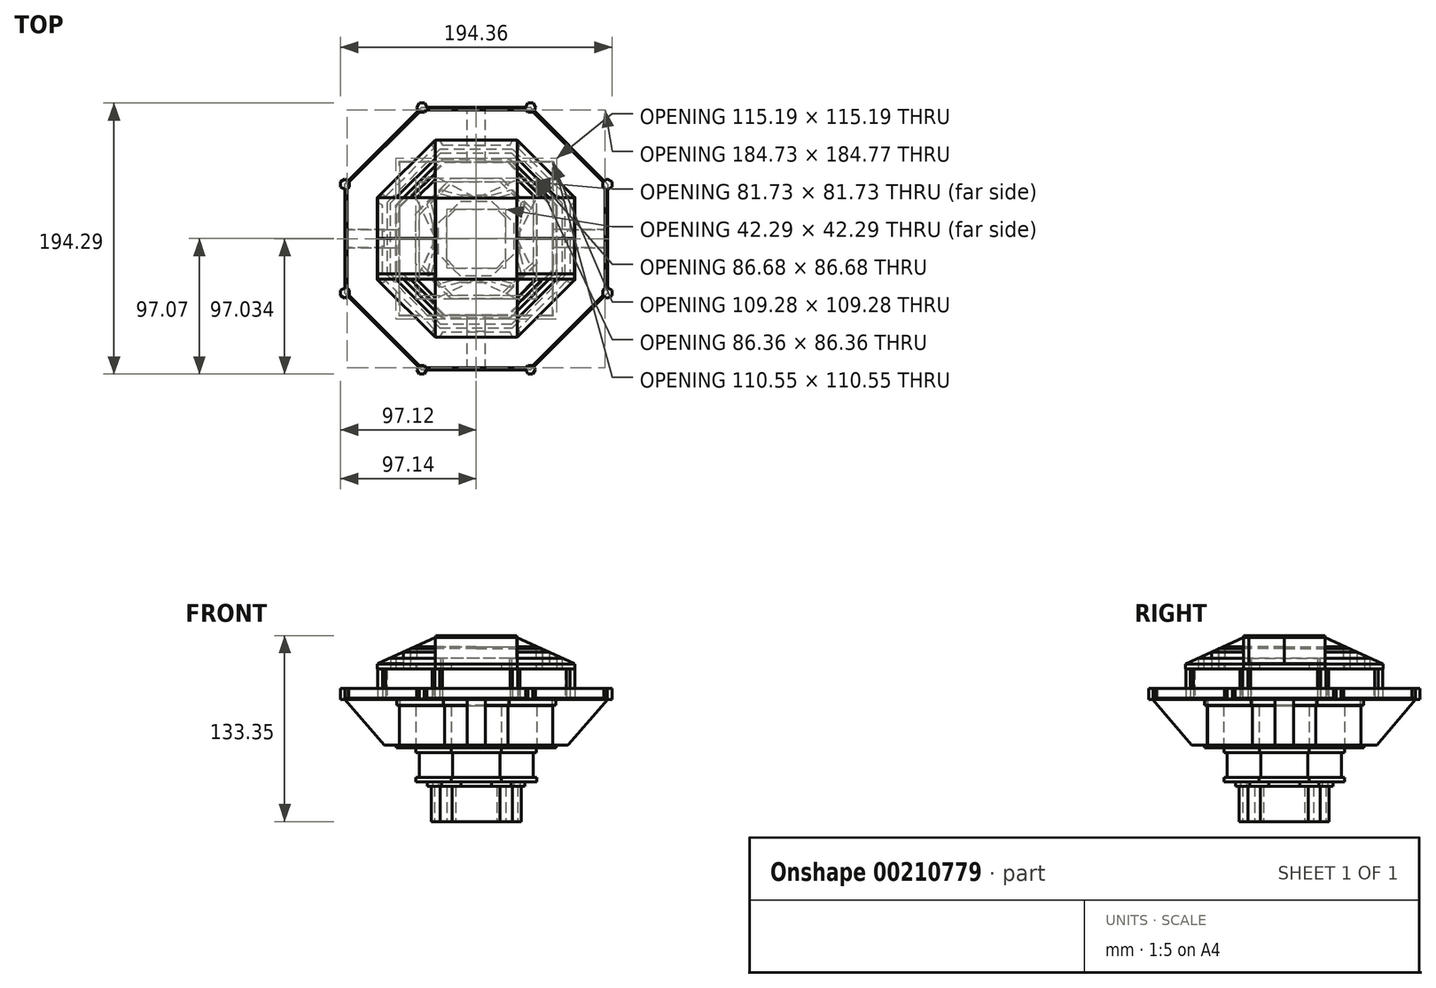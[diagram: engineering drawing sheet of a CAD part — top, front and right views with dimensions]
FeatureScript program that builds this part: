
annotation { "Feature Type Name" : "Feature", "Feature Type Description" : "" }
export const myFeature = defineFeature(function(context is Context, id is Id, definition is map)
    precondition{}
    {
        {
            var Q0;
            Q0=qCreatedBy(makeId("Top.planeOp"),FACE);
            cPlane(context, id + "F0", {"entities" : qUnion([Q0]), "cplaneType" : CPlaneType.OFFSET, "offset" : 31.24 * mm, "width" : 152.4 * mm, "height" : 152.4 * mm});
        }
        {
            var Q0;
            Q0=qCreatedBy(id+"F0.planeOp",FACE);
            cPlane(context, id + "F1", {"entities" : qUnion([Q0]), "cplaneType" : CPlaneType.OFFSET, "offset" : 19.05 * mm, "width" : 152.4 * mm, "height" : 152.4 * mm});
        }
        {
            var Q0;
            Q0=qCreatedBy(id+"F1.planeOp",FACE);
            var sketch = newSketch(context, id + "F2", { "sketchPlane" : qUnion([Q0])});
            skPoint(sketch, "E0.0.midPoint", {"position": v(0, 33.22) * mm});
            skCircle(sketch, "E1.cCircle", {"center": v(-23.49, -23.49) * mm, "radius": 7.84 * mm, "construction": true});
            skLineSegment(sketch, "E1.0", {"start": v(-25.83, -32.23) * mm, "end": v(-32.23, -25.83) * mm});
            skLineSegment(sketch, "E1.1", {"start": v(-32.23, -25.83) * mm, "end": v(-29.89, -17.09) * mm});
            skLineSegment(sketch, "E1.2", {"start": v(-29.89, -17.09) * mm, "end": v(-21.15, -14.75) * mm});
            skLineSegment(sketch, "E1.3", {"start": v(-21.15, -14.75) * mm, "end": v(-14.75, -21.15) * mm});
            skLineSegment(sketch, "E1.4", {"start": v(-14.75, -21.15) * mm, "end": v(-17.09, -29.89) * mm});
            skLineSegment(sketch, "E1.5", {"start": v(-17.09, -29.89) * mm, "end": v(-25.83, -32.23) * mm});
            skPoint(sketch, "E1.0.midPoint", {"position": v(-29.03, -29.03) * mm});
            skCircle(sketch, "E2.cCircle", {"center": v(23.49, -23.49) * mm, "radius": 7.84 * mm, "construction": true});
            skLineSegment(sketch, "E2.0", {"start": v(32.23, -25.83) * mm, "end": v(25.83, -32.23) * mm});
            skLineSegment(sketch, "E2.1", {"start": v(25.83, -32.23) * mm, "end": v(17.09, -29.89) * mm});
            skLineSegment(sketch, "E2.2", {"start": v(17.09, -29.89) * mm, "end": v(14.75, -21.15) * mm});
            skLineSegment(sketch, "E2.3", {"start": v(14.75, -21.15) * mm, "end": v(21.15, -14.75) * mm});
            skLineSegment(sketch, "E2.4", {"start": v(21.15, -14.75) * mm, "end": v(29.89, -17.09) * mm});
            skLineSegment(sketch, "E2.5", {"start": v(29.89, -17.09) * mm, "end": v(32.23, -25.83) * mm});
            skPoint(sketch, "E2.0.midPoint", {"position": v(29.03, -29.03) * mm});
            skCircle(sketch, "E3.cCircle", {"center": v(23.49, 23.49) * mm, "radius": 7.84 * mm, "construction": true});
            skLineSegment(sketch, "E3.0", {"start": v(25.83, 32.23) * mm, "end": v(32.23, 25.83) * mm});
            skLineSegment(sketch, "E3.1", {"start": v(32.23, 25.83) * mm, "end": v(29.89, 17.09) * mm});
            skLineSegment(sketch, "E3.2", {"start": v(29.89, 17.09) * mm, "end": v(21.15, 14.75) * mm});
            skLineSegment(sketch, "E3.3", {"start": v(21.15, 14.75) * mm, "end": v(14.75, 21.15) * mm});
            skLineSegment(sketch, "E3.4", {"start": v(14.75, 21.15) * mm, "end": v(17.09, 29.89) * mm});
            skLineSegment(sketch, "E3.5", {"start": v(17.09, 29.89) * mm, "end": v(25.83, 32.23) * mm});
            skPoint(sketch, "E3.0.midPoint", {"position": v(29.03, 29.03) * mm});
            skCircle(sketch, "E4.cCircle", {"center": v(-23.49, 23.49) * mm, "radius": 7.84 * mm, "construction": true});
            skLineSegment(sketch, "E4.0", {"start": v(-32.23, 25.83) * mm, "end": v(-25.83, 32.23) * mm});
            skLineSegment(sketch, "E4.1", {"start": v(-25.83, 32.23) * mm, "end": v(-17.09, 29.89) * mm});
            skLineSegment(sketch, "E4.2", {"start": v(-17.09, 29.89) * mm, "end": v(-14.75, 21.15) * mm});
            skLineSegment(sketch, "E4.3", {"start": v(-14.75, 21.15) * mm, "end": v(-21.15, 14.75) * mm});
            skLineSegment(sketch, "E4.4", {"start": v(-21.15, 14.75) * mm, "end": v(-29.89, 17.09) * mm});
            skLineSegment(sketch, "E4.5", {"start": v(-29.89, 17.09) * mm, "end": v(-32.23, 25.83) * mm});
            skPoint(sketch, "E4.0.midPoint", {"position": v(-29.03, 29.03) * mm});
            skLineSegment(sketch, "E5", {"start": v(-21.15, -14.75) * mm, "end": v(-21.15, 14.75) * mm});
            skLineSegment(sketch, "E6", {"start": v(-14.75, 21.15) * mm, "end": v(14.75, 21.15) * mm});
            skLineSegment(sketch, "E7", {"start": v(-14.75, -21.15) * mm, "end": v(14.75, -21.15) * mm});
            skLineSegment(sketch, "E8", {"start": v(21.15, -14.75) * mm, "end": v(21.15, 14.75) * mm});
            skLineSegment(sketch, "E9", {"start": v(17.09, -29.89) * mm, "end": v(-17.09, -29.89) * mm});
            skLineSegment(sketch, "E10", {"start": v(-29.89, -17.09) * mm, "end": v(-29.89, 17.09) * mm});
            skLineSegment(sketch, "E11", {"start": v(-17.09, 29.89) * mm, "end": v(17.09, 29.89) * mm});
            skLineSegment(sketch, "E12", {"start": v(29.89, 17.09) * mm, "end": v(29.89, -17.09) * mm});
            skSolve(sketch);
        }
        {
            var Q0;
            Q0=qCreatedBy(id+"F1.planeOp",FACE);
            cPlane(context, id + "F3", {"entities" : qUnion([Q0]), "cplaneType" : CPlaneType.OFFSET, "offset" : 25.4 * mm, "width" : 152.4 * mm, "height" : 152.4 * mm});
        }
        {
            var Q0;
            Q0=qCreatedBy(id+"F3.planeOp",FACE);
            var sketch = newSketch(context, id + "F4", { "sketchPlane" : qUnion([Q0])});
            skLineSegment(sketch, "E13.0", {"start": v(-12.38, 29.9) * mm, "end": v(12.38, 29.9) * mm});
            skLineSegment(sketch, "E13.2", {"start": v(29.9, 12.38) * mm, "end": v(29.9, -12.38) * mm});
            skLineSegment(sketch, "E13.4", {"start": v(12.38, -29.9) * mm, "end": v(-12.38, -29.9) * mm});
            skLineSegment(sketch, "E13.6", {"start": v(-29.9, -12.38) * mm, "end": v(-29.9, 12.38) * mm});
            skPoint(sketch, "E13.0.midPoint", {"position": v(0, 29.9) * mm});
            skLineSegment(sketch, "E14.0", {"start": v(-34.96, 24.84) * mm, "end": v(-24.84, 34.96) * mm});
            skLineSegment(sketch, "E14.1", {"start": v(-24.84, 34.96) * mm, "end": v(-11.03, 31.25) * mm});
            skLineSegment(sketch, "E14.3", {"start": v(-7.33, 17.44) * mm, "end": v(-17.44, 7.33) * mm});
            skLineSegment(sketch, "E14.5", {"start": v(-31.25, 11.03) * mm, "end": v(-34.96, 24.84) * mm});
            skPoint(sketch, "E14.0.midPoint", {"position": v(-29.9, 29.9) * mm});
            skLineSegment(sketch, "E15.0", {"start": v(24.84, 34.96) * mm, "end": v(34.96, 24.84) * mm});
            skLineSegment(sketch, "E15.1", {"start": v(34.96, 24.84) * mm, "end": v(31.25, 11.03) * mm});
            skLineSegment(sketch, "E15.3", {"start": v(17.44, 7.33) * mm, "end": v(7.33, 17.44) * mm});
            skLineSegment(sketch, "E15.5", {"start": v(11.03, 31.25) * mm, "end": v(24.84, 34.96) * mm});
            skPoint(sketch, "E15.0.midPoint", {"position": v(29.9, 29.9) * mm});
            skLineSegment(sketch, "E16.0", {"start": v(34.96, -24.84) * mm, "end": v(24.84, -34.96) * mm});
            skLineSegment(sketch, "E16.1", {"start": v(24.84, -34.96) * mm, "end": v(11.03, -31.25) * mm});
            skLineSegment(sketch, "E16.3", {"start": v(7.33, -17.44) * mm, "end": v(17.44, -7.33) * mm});
            skLineSegment(sketch, "E16.5", {"start": v(31.25, -11.03) * mm, "end": v(34.96, -24.84) * mm});
            skPoint(sketch, "E16.0.midPoint", {"position": v(29.9, -29.9) * mm});
            skLineSegment(sketch, "E17.0", {"start": v(-24.84, -34.96) * mm, "end": v(-34.96, -24.84) * mm});
            skLineSegment(sketch, "E17.1", {"start": v(-34.96, -24.84) * mm, "end": v(-31.25, -11.03) * mm});
            skLineSegment(sketch, "E17.3", {"start": v(-17.44, -7.33) * mm, "end": v(-7.33, -17.44) * mm});
            skLineSegment(sketch, "E17.5", {"start": v(-11.03, -31.25) * mm, "end": v(-24.84, -34.96) * mm});
            skPoint(sketch, "E17.0.midPoint", {"position": v(-29.9, -29.9) * mm});
            skLineSegment(sketch, "E18", {"start": v(-11.03, -31.25) * mm, "end": v(11.03, -31.25) * mm});
            skLineSegment(sketch, "E19", {"start": v(31.25, -11.03) * mm, "end": v(31.25, 11.03) * mm});
            skLineSegment(sketch, "E20", {"start": v(-11.03, 31.25) * mm, "end": v(11.03, 31.25) * mm});
            skLineSegment(sketch, "E21", {"start": v(-31.25, 11.03) * mm, "end": v(-31.25, -11.03) * mm});
            skLineSegment(sketch, "E22", {"start": v(-7.33, -17.44) * mm, "end": v(7.33, -17.44) * mm});
            skLineSegment(sketch, "E23", {"start": v(17.44, -7.33) * mm, "end": v(17.44, 7.33) * mm});
            skLineSegment(sketch, "E24", {"start": v(7.33, 17.44) * mm, "end": v(-7.33, 17.44) * mm});
            skCircle(sketch, "E25.cCircle", {"center": v(0, 0) * mm, "radius": 21.51 * mm, "construction": true});
            skPoint(sketch, "E25.cCircle.perimeterSnap0", {"position": v(17.44, 0) * mm});
            skLineSegment(sketch, "E25.0", {"start": v(21.51, 8.91) * mm, "end": v(21.51, -8.91) * mm});
            skLineSegment(sketch, "E25.1", {"start": v(21.51, -8.91) * mm, "end": v(8.91, -21.51) * mm});
            skLineSegment(sketch, "E25.2", {"start": v(8.91, -21.51) * mm, "end": v(-8.91, -21.51) * mm});
            skLineSegment(sketch, "E25.4", {"start": v(-21.51, -8.91) * mm, "end": v(-21.51, 8.91) * mm});
            skLineSegment(sketch, "E25.5", {"start": v(-21.51, 8.91) * mm, "end": v(-8.91, 21.51) * mm});
            skLineSegment(sketch, "E25.6", {"start": v(-8.91, 21.51) * mm, "end": v(8.91, 21.51) * mm});
            skLineSegment(sketch, "E25.7", {"start": v(8.91, 21.51) * mm, "end": v(21.51, 8.91) * mm});
            skPoint(sketch, "E25.0.midPoint", {"position": v(21.51, 0) * mm});
            skPoint(sketch, "E25.0.midPoint.positionSnap0", {"position": v(17.44, 0) * mm});
            skCircle(sketch, "E26.cCircle", {"center": v(0, 0) * mm, "radius": 26.95 * mm, "construction": true});
            skPoint(sketch, "E26.cCircle.perimeterSnap0", {"position": v(0, 21.51) * mm});
            skLineSegment(sketch, "E26.0", {"start": v(-11.16, 26.95) * mm, "end": v(11.16, 26.95) * mm});
            skLineSegment(sketch, "E26.1", {"start": v(11.16, 26.95) * mm, "end": v(26.95, 11.16) * mm});
            skLineSegment(sketch, "E26.2", {"start": v(26.95, 11.16) * mm, "end": v(26.95, -11.16) * mm});
            skLineSegment(sketch, "E26.3", {"start": v(26.95, -11.16) * mm, "end": v(11.16, -26.95) * mm});
            skLineSegment(sketch, "E26.4", {"start": v(11.16, -26.95) * mm, "end": v(-11.16, -26.95) * mm});
            skLineSegment(sketch, "E26.5", {"start": v(-11.16, -26.95) * mm, "end": v(-26.95, -11.16) * mm});
            skLineSegment(sketch, "E26.6", {"start": v(-26.95, -11.16) * mm, "end": v(-26.95, 11.16) * mm});
            skLineSegment(sketch, "E26.7", {"start": v(-26.95, 11.16) * mm, "end": v(-11.16, 26.95) * mm});
            skPoint(sketch, "E26.0.midPoint", {"position": v(0, 26.95) * mm});
            skPoint(sketch, "E26.0.midPoint.positionSnap0", {"position": v(0, 21.51) * mm});
            skSolve(sketch);
        }
        {
            var Q0;
            Q0=qSketchRegion(id+"F2",true);
            extrude(context, id + "F5", {"entities" : qUnion([Q0]), "depth" : 25.4 * mm});
        }
        {
            var Q0;
            Q0=qSketchRegion(id+"F4",true);
            extrude(context, id + "F6", {"entities" : qUnion([Q0]), "operationType" : NewBodyOperationType.ADD, "depth" : 3.05 * mm});
        }
        {
            var Q0;
            Q0=qCreatedBy(id+"F3.planeOp",FACE);
            cPlane(context, id + "F7", {"entities" : qUnion([Q0]), "cplaneType" : CPlaneType.OFFSET, "offset" : 3.05 * mm, "width" : 152.4 * mm, "height" : 152.4 * mm});
        }
        {
            var Q0;
            Q0=qCreatedBy(id+"F7.planeOp",FACE);
            var sketch = newSketch(context, id + "F8", { "sketchPlane" : qUnion([Q0])});
            skCircle(sketch, "E27.cCircle", {"center": v(0, 0) * mm, "radius": 43.28 * mm, "construction": true});
            skLineSegment(sketch, "E27.0", {"start": v(-17.93, 43.28) * mm, "end": v(17.93, 43.28) * mm});
            skLineSegment(sketch, "E27.1", {"start": v(17.93, 43.28) * mm, "end": v(43.28, 17.93) * mm});
            skLineSegment(sketch, "E27.2", {"start": v(43.28, 17.93) * mm, "end": v(43.28, -17.93) * mm});
            skLineSegment(sketch, "E27.3", {"start": v(43.28, -17.93) * mm, "end": v(17.93, -43.28) * mm});
            skLineSegment(sketch, "E27.4", {"start": v(17.93, -43.28) * mm, "end": v(-17.93, -43.28) * mm});
            skLineSegment(sketch, "E27.5", {"start": v(-17.93, -43.28) * mm, "end": v(-43.28, -17.93) * mm});
            skLineSegment(sketch, "E27.6", {"start": v(-43.28, -17.93) * mm, "end": v(-43.28, 17.93) * mm});
            skLineSegment(sketch, "E27.7", {"start": v(-43.28, 17.93) * mm, "end": v(-17.93, 43.28) * mm});
            skPoint(sketch, "E27.0.midPoint", {"position": v(0, 43.28) * mm});
            skSolve(sketch);
        }
        {
            var Q0;
            Q0 = qSketchRegion(id + "F8", true);
            extrude(context, id + "F9", {"entities" : qUnion([Q0]), "operationType" : NewBodyOperationType.ADD, "depth" : 3.3 * mm});
        }
        {
            var Q0;
            Q0=qCreatedBy(id+"F3.planeOp",FACE);
            cPlane(context, id + "F10", {"entities" : qUnion([Q0]), "cplaneType" : CPlaneType.OFFSET, "offset" : 6.35 * mm, "width" : 152.4 * mm, "height" : 152.4 * mm});
        }
        {
            var Q0;
            Q0=qCreatedBy(id+"F10.planeOp",FACE);
            var sketch = newSketch(context, id + "F11", { "sketchPlane" : qUnion([Q0])});
            skCircle(sketch, "E28.cCircle", {"center": v(0, 0) * mm, "radius": 40.86 * mm, "construction": true});
            skLineSegment(sketch, "E28.0", {"start": v(-16.93, 40.86) * mm, "end": v(16.93, 40.86) * mm});
            skLineSegment(sketch, "E28.1", {"start": v(16.93, 40.86) * mm, "end": v(40.86, 16.93) * mm});
            skLineSegment(sketch, "E28.2", {"start": v(40.86, 16.93) * mm, "end": v(40.86, -16.93) * mm});
            skLineSegment(sketch, "E28.3", {"start": v(40.86, -16.93) * mm, "end": v(16.93, -40.86) * mm});
            skLineSegment(sketch, "E28.4", {"start": v(16.93, -40.86) * mm, "end": v(-16.93, -40.86) * mm});
            skLineSegment(sketch, "E28.5", {"start": v(-16.93, -40.86) * mm, "end": v(-40.86, -16.93) * mm});
            skLineSegment(sketch, "E28.6", {"start": v(-40.86, -16.93) * mm, "end": v(-40.86, 16.93) * mm});
            skLineSegment(sketch, "E28.7", {"start": v(-40.86, 16.93) * mm, "end": v(-16.93, 40.86) * mm});
            skPoint(sketch, "E28.0.midPoint", {"position": v(0, 40.86) * mm});
            skSolve(sketch);
        }
        {
            var Q0;
            Q0 = qSketchRegion(id + "F11", true);
            extrude(context, id + "F12", {"entities" : qUnion([Q0]), "operationType" : NewBodyOperationType.ADD, "depth" : 18.03 * mm});
        }
        {
            var Q0;
            Q0=qCreatedBy(id+"F10.planeOp",FACE);
            cPlane(context, id + "F13", {"entities" : qUnion([Q0]), "cplaneType" : CPlaneType.OFFSET, "offset" : 17.78 * mm, "width" : 152.4 * mm, "height" : 152.4 * mm});
        }
        {
            var Q0;
            Q0=qCreatedBy(id+"F13.planeOp",FACE);
            var sketch = newSketch(context, id + "F14", { "sketchPlane" : qUnion([Q0])});
            skCircle(sketch, "E29.cCircle", {"center": v(0, 0) * mm, "radius": 43.18 * mm, "construction": true});
            skLineSegment(sketch, "E29.0", {"start": v(43.18, 17.89) * mm, "end": v(43.18, -17.89) * mm});
            skLineSegment(sketch, "E29.1", {"start": v(43.18, -17.89) * mm, "end": v(17.89, -43.18) * mm});
            skLineSegment(sketch, "E29.2", {"start": v(17.89, -43.18) * mm, "end": v(-17.89, -43.18) * mm});
            skLineSegment(sketch, "E29.3", {"start": v(-17.89, -43.18) * mm, "end": v(-43.18, -17.89) * mm});
            skLineSegment(sketch, "E29.4", {"start": v(-43.18, -17.89) * mm, "end": v(-43.18, 17.89) * mm});
            skLineSegment(sketch, "E29.5", {"start": v(-43.18, 17.89) * mm, "end": v(-17.89, 43.18) * mm});
            skLineSegment(sketch, "E29.6", {"start": v(-17.89, 43.18) * mm, "end": v(17.89, 43.18) * mm});
            skLineSegment(sketch, "E29.7", {"start": v(17.89, 43.18) * mm, "end": v(43.18, 17.89) * mm});
            skPoint(sketch, "E29.0.midPoint", {"position": v(43.18, 0) * mm});
            skSolve(sketch);
        }
        {
            var Q0;
            Q0 = qSketchRegion(id + "F14", true);
            extrude(context, id + "F15", {"entities" : qUnion([Q0]), "operationType" : NewBodyOperationType.ADD, "depth" : 3.3 * mm});
        }
        {
            var Q0;
            Q0=qCreatedBy(id+"F13.planeOp",FACE);
            cPlane(context, id + "F16", {"entities" : qUnion([Q0]), "cplaneType" : CPlaneType.OFFSET, "offset" : 3.3 * mm, "width" : 152.4 * mm, "height" : 152.4 * mm});
        }
        {
            var Q0;
            Q0=qCreatedBy(id+"F16.planeOp",FACE);
            var sketch = newSketch(context, id + "F17", { "sketchPlane" : qUnion([Q0])});
            skLineSegment(sketch, "E30.0", {"start": v(43.34, 17.95) * mm, "end": v(43.34, -17.95) * mm});
            skLineSegment(sketch, "E30.1", {"start": v(43.34, -17.95) * mm, "end": v(17.95, -43.34) * mm});
            skLineSegment(sketch, "E30.2", {"start": v(17.95, -43.34) * mm, "end": v(-17.95, -43.34) * mm});
            skLineSegment(sketch, "E30.3", {"start": v(-17.95, -43.34) * mm, "end": v(-43.34, -17.95) * mm});
            skLineSegment(sketch, "E30.4", {"start": v(-43.34, -17.95) * mm, "end": v(-43.34, 17.95) * mm});
            skLineSegment(sketch, "E30.5", {"start": v(-43.34, 17.95) * mm, "end": v(-17.95, 43.34) * mm});
            skLineSegment(sketch, "E30.6", {"start": v(-17.95, 43.34) * mm, "end": v(17.95, 43.34) * mm});
            skLineSegment(sketch, "E30.7", {"start": v(17.95, 43.34) * mm, "end": v(43.34, 17.95) * mm});
            skPoint(sketch, "E30.0.midPoint", {"position": v(43.34, 0) * mm});
            skLineSegment(sketch, "E31.0", {"start": v(54.86, 22.72) * mm, "end": v(54.86, -22.72) * mm});
            skLineSegment(sketch, "E31.1", {"start": v(54.86, -22.72) * mm, "end": v(22.72, -54.86) * mm});
            skLineSegment(sketch, "E31.2", {"start": v(22.72, -54.86) * mm, "end": v(-22.72, -54.86) * mm});
            skLineSegment(sketch, "E31.3", {"start": v(-22.72, -54.86) * mm, "end": v(-54.86, -22.72) * mm});
            skLineSegment(sketch, "E31.4", {"start": v(-54.86, -22.72) * mm, "end": v(-54.86, 22.72) * mm});
            skLineSegment(sketch, "E31.5", {"start": v(-54.86, 22.72) * mm, "end": v(-22.72, 54.86) * mm});
            skLineSegment(sketch, "E31.6", {"start": v(-22.72, 54.86) * mm, "end": v(22.72, 54.86) * mm});
            skLineSegment(sketch, "E31.7", {"start": v(22.72, 54.86) * mm, "end": v(54.86, 22.72) * mm});
            skPoint(sketch, "E31.0.midPoint", {"position": v(54.86, 0) * mm});
            skLineSegment(sketch, "E32.0", {"start": v(43.34, -6.65) * mm, "end": v(43.34, 6.65) * mm});
            skLineSegment(sketch, "E33.0", {"start": v(-6.65, -43.34) * mm, "end": v(6.65, -43.34) * mm});
            skPoint(sketch, "E33.0.midPoint", {"position": v(0, -43.34) * mm});
            skLineSegment(sketch, "E34.0", {"start": v(-43.34, 6.65) * mm, "end": v(-43.34, -6.65) * mm});
            skPoint(sketch, "E34.0.midPoint", {"position": v(-43.34, 0) * mm});
            skLineSegment(sketch, "E35.0", {"start": v(6.65, 43.34) * mm, "end": v(-6.65, 43.34) * mm});
            skPoint(sketch, "E35.0.midPoint", {"position": v(0, 43.34) * mm});
            skLineSegment(sketch, "E36.right", {"start": v(43.34, 6.65) * mm, "end": v(43.34, -6.65) * mm});
            skLineSegment(sketch, "E37.top", {"start": v(6.65, -43.34) * mm, "end": v(-6.65, -43.34) * mm});
            skLineSegment(sketch, "E38.top", {"start": v(-6.65, 43.34) * mm, "end": v(6.65, 43.34) * mm});
            skSolve(sketch);
        }
        {
            var Q0;
            Q0 = qSketchRegion(id + "F17", true);
            extrude(context, id + "F18", {"entities" : qUnion([Q0]), "depth" : 30.23 * mm});
        }
        {
            var Q0;
            Q0=qCreatedBy(makeId("Front.planeOp"),FACE);
            var sketch = newSketch(context, id + "F19", { "sketchPlane" : qUnion([Q0])});
            skLineSegment(sketch, "E39.left", {"start": v(66.19, 105.71) * mm, "end": v(66.19, 105.71) * mm});
            skLineSegment(sketch, "E39.right", {"start": v(-66.19, 105.71) * mm, "end": v(-66.19, 105.71) * mm});
            skLineSegment(sketch, "E40", {"start": v(66.19, 105.71) * mm, "end": v(94.2, 137.85) * mm});
            skLineSegment(sketch, "E41", {"start": v(-66.19, 105.71) * mm, "end": v(-94.2, 137.85) * mm});
            skLineSegment(sketch, "E42.bottom", {"start": v(94.2, 137.85) * mm, "end": v(55.17, 137.85) * mm});
            skLineSegment(sketch, "E42.right", {"start": v(55.17, 137.85) * mm, "end": v(55.17, 105.71) * mm});
            skLineSegment(sketch, "E43.bottom", {"start": v(-94.2, 137.85) * mm, "end": v(-54.57, 137.85) * mm});
            skLineSegment(sketch, "E43.right", {"start": v(-54.57, 137.85) * mm, "end": v(-54.57, 105.71) * mm});
            skLineSegment(sketch, "E44", {"start": v(66.19, 105.71) * mm, "end": v(55.17, 105.71) * mm});
            skLineSegment(sketch, "E45", {"start": v(-54.57, 105.71) * mm, "end": v(-66.19, 105.71) * mm});
            skLineSegment(sketch, "E46", {"start": v(-66.19, 105.71) * mm, "end": v(-65.35, 104.75) * mm});
            skLineSegment(sketch, "E47", {"start": v(-54.57, 104.75) * mm, "end": v(-54.57, 105.71) * mm});
            skLineSegment(sketch, "E48", {"start": v(66.19, 105.71) * mm, "end": v(65.36, 104.75) * mm});
            skLineSegment(sketch, "E49", {"start": v(55.17, 104.75) * mm, "end": v(55.17, 105.71) * mm});
            skLineSegment(sketch, "E50", {"start": v(54.86, 104.75) * mm, "end": v(54.86, 137.85) * mm});
            skLineSegment(sketch, "E51", {"start": v(54.86, 137.85) * mm, "end": v(55.17, 137.85) * mm});
            skLineSegment(sketch, "E52", {"start": v(65.77, 105.23) * mm, "end": v(55.17, 105.23) * mm});
            skLineSegment(sketch, "E53", {"start": v(55.17, 105.23) * mm, "end": v(54.86, 105.23) * mm});
            skLineSegment(sketch, "E54", {"start": v(-65.77, 105.23) * mm, "end": v(-54.57, 105.23) * mm});
            skSolve(sketch);
        }
        {
            var Q0;
            Q0 = qSketchRegion(id + "F19", true);
            extrude(context, id + "F20", {"entities" : qUnion([Q0]), "endBound" : BoundingType.SYMMETRIC, "depth" : 13.2 * mm});
        }
        {
            var Q0;
            Q0=qCreatedBy(id+"F16.planeOp",FACE);
            cPlane(context, id + "F21", {"entities" : qUnion([Q0]), "cplaneType" : CPlaneType.OFFSET, "offset" : 34.8 * mm, "width" : 152.4 * mm, "height" : 152.4 * mm});
        }
        {
            var Q0;
            Q0=qCreatedBy(id+"F21.planeOp",FACE);
            var sketch = newSketch(context, id + "F22", { "sketchPlane" : qUnion([Q0])});
            skCircle(sketch, "E55.cCircle", {"center": v(0, 0) * mm, "radius": 94.16 * mm, "construction": true});
            skLineSegment(sketch, "E55.0", {"start": v(94.16, 39) * mm, "end": v(94.16, -39) * mm});
            skLineSegment(sketch, "E55.1", {"start": v(94.16, -39) * mm, "end": v(39, -94.16) * mm});
            skLineSegment(sketch, "E55.2", {"start": v(39, -94.16) * mm, "end": v(-39, -94.16) * mm});
            skLineSegment(sketch, "E55.3", {"start": v(-39, -94.16) * mm, "end": v(-94.16, -39) * mm});
            skLineSegment(sketch, "E55.4", {"start": v(-94.16, -39) * mm, "end": v(-94.16, 39) * mm});
            skLineSegment(sketch, "E55.5", {"start": v(-94.16, 39) * mm, "end": v(-39, 94.16) * mm});
            skLineSegment(sketch, "E55.6", {"start": v(-39, 94.16) * mm, "end": v(39, 94.16) * mm});
            skLineSegment(sketch, "E55.7", {"start": v(39, 94.16) * mm, "end": v(94.16, 39) * mm});
            skPoint(sketch, "E55.0.midPoint", {"position": v(94.16, 0) * mm});
            skCircle(sketch, "E56.cCircle", {"center": v(0, 0) * mm, "radius": 55.27 * mm, "construction": true});
            skLineSegment(sketch, "E56.0", {"start": v(-22.9, 55.27) * mm, "end": v(22.9, 55.27) * mm});
            skLineSegment(sketch, "E56.1", {"start": v(22.9, 55.27) * mm, "end": v(55.27, 22.9) * mm});
            skLineSegment(sketch, "E56.2", {"start": v(55.27, 22.9) * mm, "end": v(55.27, -22.9) * mm});
            skLineSegment(sketch, "E56.3", {"start": v(55.27, -22.9) * mm, "end": v(22.9, -55.27) * mm});
            skLineSegment(sketch, "E56.4", {"start": v(22.9, -55.27) * mm, "end": v(-22.9, -55.27) * mm});
            skLineSegment(sketch, "E56.5", {"start": v(-22.9, -55.27) * mm, "end": v(-55.27, -22.9) * mm});
            skLineSegment(sketch, "E56.6", {"start": v(-55.27, -22.9) * mm, "end": v(-55.27, 22.9) * mm});
            skLineSegment(sketch, "E56.7", {"start": v(-55.27, 22.9) * mm, "end": v(-22.9, 55.27) * mm});
            skPoint(sketch, "E56.0.midPoint", {"position": v(0, 55.27) * mm});
            skSolve(sketch);
        }
        {
            var Q0;
            Q0 = qSketchRegion(id + "F22", true);
            extrude(context, id + "F23", {"entities" : qUnion([Q0]), "depth" : 1.02 * mm});
        }
        {
            var Q0;
            Q0=qCreatedBy(makeId("Right.planeOp"),FACE);
            var sketch = newSketch(context, id + "F24", { "sketchPlane" : qUnion([Q0])});
            skLineSegment(sketch, "E57", {"start": v(0, 74.17) * mm, "end": v(0, 105.16) * mm});
            skPoint(sketch, "E58.middle", {"position": v(0, 105.16) * mm});
            skLineSegment(sketch, "E59.left", {"start": v(-66.36, 105.16) * mm, "end": v(-66.36, 105.16) * mm});
            skLineSegment(sketch, "E59.right", {"start": v(66.36, 105.16) * mm, "end": v(66.36, 105.16) * mm});
            skLineSegment(sketch, "E60", {"start": v(-94.16, 137.92) * mm, "end": v(-66.36, 105.16) * mm});
            skLineSegment(sketch, "E61", {"start": v(66.36, 105.16) * mm, "end": v(94.16, 137.92) * mm});
            skLineSegment(sketch, "E62", {"start": v(-55.21, 105.16) * mm, "end": v(-55.21, 137.92) * mm});
            skLineSegment(sketch, "E63", {"start": v(54.83, 105.16) * mm, "end": v(54.83, 137.92) * mm});
            skLineSegment(sketch, "E64", {"start": v(-66.36, 105.16) * mm, "end": v(-55.21, 105.16) * mm});
            skLineSegment(sketch, "E65", {"start": v(-94.16, 137.92) * mm, "end": v(-55.21, 137.92) * mm});
            skLineSegment(sketch, "E66", {"start": v(54.83, 105.16) * mm, "end": v(66.36, 105.16) * mm});
            skLineSegment(sketch, "E67", {"start": v(54.83, 137.92) * mm, "end": v(94.16, 137.92) * mm});
            skSolve(sketch);
        }
        {
            var Q0;
            Q0 = qSketchRegion(id + "F24", true);
            extrude(context, id + "F25", {"entities" : qUnion([Q0]), "endBound" : BoundingType.SYMMETRIC, "depth" : 13.2 * mm});
        }
        {
            var Q0;
            Q0=qCreatedBy(id+"F21.planeOp",FACE);
            var sketch = newSketch(context, id + "F26", { "sketchPlane" : qUnion([Q0])});
            skCircle(sketch, "E68.cCircle", {"center": v(0, 0) * mm, "radius": 57 * mm, "construction": true});
            skLineSegment(sketch, "E68.0", {"start": v(-23.6, 57) * mm, "end": v(23.6, 57) * mm});
            skLineSegment(sketch, "E68.1", {"start": v(23.6, 57) * mm, "end": v(57, 23.6) * mm});
            skLineSegment(sketch, "E68.2", {"start": v(57, 23.6) * mm, "end": v(57, -23.6) * mm});
            skLineSegment(sketch, "E68.3", {"start": v(57, -23.6) * mm, "end": v(23.6, -57) * mm});
            skLineSegment(sketch, "E68.4", {"start": v(23.6, -57) * mm, "end": v(-23.6, -57) * mm});
            skLineSegment(sketch, "E68.5", {"start": v(-23.6, -57) * mm, "end": v(-57, -23.6) * mm});
            skLineSegment(sketch, "E68.6", {"start": v(-57, -23.6) * mm, "end": v(-57, 23.6) * mm});
            skLineSegment(sketch, "E68.7", {"start": v(-57, 23.6) * mm, "end": v(-23.6, 57) * mm});
            skPoint(sketch, "E68.0.midPoint", {"position": v(0, 57) * mm});
            skCircle(sketch, "E69.cCircle", {"center": v(0, 0) * mm, "radius": 54.64 * mm, "construction": true});
            skLineSegment(sketch, "E69.0", {"start": v(-22.63, 54.64) * mm, "end": v(22.63, 54.64) * mm});
            skLineSegment(sketch, "E69.1", {"start": v(22.63, 54.64) * mm, "end": v(54.64, 22.63) * mm});
            skLineSegment(sketch, "E69.2", {"start": v(54.64, 22.63) * mm, "end": v(54.64, -22.63) * mm});
            skLineSegment(sketch, "E69.3", {"start": v(54.64, -22.63) * mm, "end": v(22.63, -54.64) * mm});
            skLineSegment(sketch, "E69.4", {"start": v(22.63, -54.64) * mm, "end": v(-22.63, -54.64) * mm});
            skLineSegment(sketch, "E69.5", {"start": v(-22.63, -54.64) * mm, "end": v(-54.64, -22.63) * mm});
            skLineSegment(sketch, "E69.6", {"start": v(-54.64, -22.63) * mm, "end": v(-54.64, 22.63) * mm});
            skLineSegment(sketch, "E69.7", {"start": v(-54.64, 22.63) * mm, "end": v(-22.63, 54.64) * mm});
            skPoint(sketch, "E69.0.midPoint", {"position": v(0, 54.64) * mm});
            skSolve(sketch);
        }
        {
            var Q0;
            Q0 = qSketchRegion(id + "F26", true);
            extrude(context, id + "F27", {"entities" : qUnion([Q0]), "oppositeDirection" : true, "depth" : 4.32 * mm});
        }
        {
            var Q0;
            Q0=qCreatedBy(id+"F16.planeOp",FACE);
            var sketch = newSketch(context, id + "F28", { "sketchPlane" : qUnion([Q0])});
            skCircle(sketch, "E70.cCircle", {"center": v(0, 0) * mm, "radius": 57.26 * mm, "construction": true});
            skLineSegment(sketch, "E70.0", {"start": v(-23.72, 57.26) * mm, "end": v(23.72, 57.26) * mm});
            skLineSegment(sketch, "E70.1", {"start": v(23.72, 57.26) * mm, "end": v(57.26, 23.72) * mm});
            skLineSegment(sketch, "E70.2", {"start": v(57.26, 23.72) * mm, "end": v(57.26, -23.72) * mm});
            skLineSegment(sketch, "E70.3", {"start": v(57.26, -23.72) * mm, "end": v(23.72, -57.26) * mm});
            skLineSegment(sketch, "E70.4", {"start": v(23.72, -57.26) * mm, "end": v(-23.72, -57.26) * mm});
            skLineSegment(sketch, "E70.5", {"start": v(-23.72, -57.26) * mm, "end": v(-57.26, -23.72) * mm});
            skLineSegment(sketch, "E70.6", {"start": v(-57.26, -23.72) * mm, "end": v(-57.26, 23.72) * mm});
            skLineSegment(sketch, "E70.7", {"start": v(-57.26, 23.72) * mm, "end": v(-23.72, 57.26) * mm});
            skPoint(sketch, "E70.0.midPoint", {"position": v(0, 57.26) * mm});
            skSolve(sketch);
        }
        {
            var Q0;
            Q0 = qSketchRegion(id + "F28", true);
            extrude(context, id + "F29", {"entities" : qUnion([Q0]), "depth" : 2.03 * mm});
        }
        {
            var Q0;
            Q0=qCreatedBy(id+"F21.planeOp",FACE);
            var sketch = newSketch(context, id + "F30", { "sketchPlane" : qUnion([Q0])});
            skLineSegment(sketch, "E71.0", {"start": v(-38.92, 93.97) * mm, "end": v(38.92, 93.97) * mm});
            skLineSegment(sketch, "E71.1", {"start": v(38.92, 93.97) * mm, "end": v(93.97, 38.92) * mm});
            skLineSegment(sketch, "E71.2", {"start": v(93.97, 38.92) * mm, "end": v(93.97, -38.92) * mm});
            skLineSegment(sketch, "E71.3", {"start": v(93.97, -38.92) * mm, "end": v(38.92, -93.97) * mm});
            skLineSegment(sketch, "E71.4", {"start": v(38.92, -93.97) * mm, "end": v(-38.92, -93.97) * mm});
            skLineSegment(sketch, "E71.5", {"start": v(-38.92, -93.97) * mm, "end": v(-93.97, -38.92) * mm});
            skLineSegment(sketch, "E71.6", {"start": v(-93.97, -38.92) * mm, "end": v(-93.97, 38.92) * mm});
            skLineSegment(sketch, "E71.7", {"start": v(-93.97, 38.92) * mm, "end": v(-38.92, 93.97) * mm});
            skPoint(sketch, "E71.0.midPoint", {"position": v(0, 93.97) * mm});
            skCircle(sketch, "E72.cCircle", {"center": v(-38.92, -93.97) * mm, "radius": 3.1 * mm, "construction": true});
            skLineSegment(sketch, "E72.0", {"start": v(-40.71, -90.87) * mm, "end": v(-37.13, -90.87) * mm});
            skLineSegment(sketch, "E72.1", {"start": v(-37.13, -90.87) * mm, "end": v(-35.34, -93.97) * mm});
            skLineSegment(sketch, "E72.2", {"start": v(-35.34, -93.97) * mm, "end": v(-37.13, -97.07) * mm});
            skLineSegment(sketch, "E72.3", {"start": v(-37.13, -97.07) * mm, "end": v(-40.71, -97.07) * mm});
            skLineSegment(sketch, "E72.4", {"start": v(-40.71, -97.07) * mm, "end": v(-42.5, -93.97) * mm});
            skLineSegment(sketch, "E72.5", {"start": v(-42.5, -93.97) * mm, "end": v(-40.71, -90.87) * mm});
            skPoint(sketch, "E72.0.midPoint", {"position": v(-38.92, -90.87) * mm});
            skCircle(sketch, "E73.cCircle", {"center": v(38.92, -93.97) * mm, "radius": 3.1 * mm, "construction": true});
            skLineSegment(sketch, "E73.0", {"start": v(37.13, -90.87) * mm, "end": v(40.71, -90.87) * mm});
            skLineSegment(sketch, "E73.1", {"start": v(40.71, -90.87) * mm, "end": v(42.5, -93.97) * mm});
            skLineSegment(sketch, "E73.2", {"start": v(42.5, -93.97) * mm, "end": v(40.71, -97.07) * mm});
            skLineSegment(sketch, "E73.3", {"start": v(40.71, -97.07) * mm, "end": v(37.13, -97.07) * mm});
            skLineSegment(sketch, "E73.4", {"start": v(37.13, -97.07) * mm, "end": v(35.34, -93.97) * mm});
            skLineSegment(sketch, "E73.5", {"start": v(35.34, -93.97) * mm, "end": v(37.13, -90.87) * mm});
            skPoint(sketch, "E73.0.midPoint", {"position": v(38.92, -90.87) * mm});
            skCircle(sketch, "E74.cCircle", {"center": v(93.97, -38.92) * mm, "radius": 3.25 * mm, "construction": true});
            skLineSegment(sketch, "E74.0", {"start": v(90.72, -40.8) * mm, "end": v(90.72, -37.05) * mm});
            skLineSegment(sketch, "E74.1", {"start": v(90.72, -37.05) * mm, "end": v(93.97, -35.17) * mm});
            skLineSegment(sketch, "E74.2", {"start": v(93.97, -35.17) * mm, "end": v(97.22, -37.05) * mm});
            skLineSegment(sketch, "E74.3", {"start": v(97.22, -37.05) * mm, "end": v(97.22, -40.8) * mm});
            skLineSegment(sketch, "E74.4", {"start": v(97.22, -40.8) * mm, "end": v(93.97, -42.68) * mm});
            skLineSegment(sketch, "E74.5", {"start": v(93.97, -42.68) * mm, "end": v(90.72, -40.8) * mm});
            skPoint(sketch, "E74.0.midPoint", {"position": v(90.72, -38.92) * mm});
            skCircle(sketch, "E75.cCircle", {"center": v(93.97, 38.92) * mm, "radius": 3.25 * mm, "construction": true});
            skLineSegment(sketch, "E75.0", {"start": v(90.72, 37.05) * mm, "end": v(90.72, 40.8) * mm});
            skLineSegment(sketch, "E75.1", {"start": v(90.72, 40.8) * mm, "end": v(93.97, 42.68) * mm});
            skLineSegment(sketch, "E75.2", {"start": v(93.97, 42.68) * mm, "end": v(97.22, 40.8) * mm});
            skLineSegment(sketch, "E75.3", {"start": v(97.22, 40.8) * mm, "end": v(97.22, 37.05) * mm});
            skLineSegment(sketch, "E75.4", {"start": v(97.22, 37.05) * mm, "end": v(93.97, 35.17) * mm});
            skLineSegment(sketch, "E75.5", {"start": v(93.97, 35.17) * mm, "end": v(90.72, 37.05) * mm});
            skPoint(sketch, "E75.0.midPoint", {"position": v(90.72, 38.92) * mm});
            skCircle(sketch, "E76.cCircle", {"center": v(-93.97, -38.92) * mm, "radius": 3.17 * mm, "construction": true});
            skLineSegment(sketch, "E76.0", {"start": v(-90.8, -37.1) * mm, "end": v(-90.8, -40.76) * mm});
            skLineSegment(sketch, "E76.1", {"start": v(-90.8, -40.76) * mm, "end": v(-93.97, -42.59) * mm});
            skLineSegment(sketch, "E76.2", {"start": v(-93.97, -42.59) * mm, "end": v(-97.14, -40.76) * mm});
            skLineSegment(sketch, "E76.3", {"start": v(-97.14, -40.76) * mm, "end": v(-97.14, -37.1) * mm});
            skLineSegment(sketch, "E76.4", {"start": v(-97.14, -37.1) * mm, "end": v(-93.97, -35.26) * mm});
            skLineSegment(sketch, "E76.5", {"start": v(-93.97, -35.26) * mm, "end": v(-90.8, -37.1) * mm});
            skPoint(sketch, "E76.0.midPoint", {"position": v(-90.8, -38.92) * mm});
            skCircle(sketch, "E77.cCircle", {"center": v(-93.97, 38.92) * mm, "radius": 3.17 * mm, "construction": true});
            skLineSegment(sketch, "E77.0", {"start": v(-90.8, 40.76) * mm, "end": v(-90.8, 37.1) * mm});
            skLineSegment(sketch, "E77.1", {"start": v(-90.8, 37.1) * mm, "end": v(-93.97, 35.26) * mm});
            skLineSegment(sketch, "E77.2", {"start": v(-93.97, 35.26) * mm, "end": v(-97.14, 37.1) * mm});
            skLineSegment(sketch, "E77.3", {"start": v(-97.14, 37.1) * mm, "end": v(-97.14, 40.76) * mm});
            skLineSegment(sketch, "E77.4", {"start": v(-97.14, 40.76) * mm, "end": v(-93.97, 42.59) * mm});
            skLineSegment(sketch, "E77.5", {"start": v(-93.97, 42.59) * mm, "end": v(-90.8, 40.76) * mm});
            skPoint(sketch, "E77.0.midPoint", {"position": v(-90.8, 38.92) * mm});
            skCircle(sketch, "E78.cCircle", {"center": v(-38.92, 93.97) * mm, "radius": 3.25 * mm, "construction": true});
            skLineSegment(sketch, "E78.0", {"start": v(-37.05, 90.72) * mm, "end": v(-40.8, 90.72) * mm});
            skLineSegment(sketch, "E78.1", {"start": v(-40.8, 90.72) * mm, "end": v(-42.67, 93.97) * mm});
            skLineSegment(sketch, "E78.2", {"start": v(-42.67, 93.97) * mm, "end": v(-40.8, 97.22) * mm});
            skLineSegment(sketch, "E78.3", {"start": v(-40.8, 97.22) * mm, "end": v(-37.05, 97.22) * mm});
            skLineSegment(sketch, "E78.4", {"start": v(-37.05, 97.22) * mm, "end": v(-35.18, 93.97) * mm});
            skLineSegment(sketch, "E78.5", {"start": v(-35.18, 93.97) * mm, "end": v(-37.05, 90.72) * mm});
            skPoint(sketch, "E78.0.midPoint", {"position": v(-38.92, 90.72) * mm});
            skCircle(sketch, "E79.cCircle", {"center": v(38.92, 93.97) * mm, "radius": 3.25 * mm, "construction": true});
            skLineSegment(sketch, "E79.0", {"start": v(40.8, 90.72) * mm, "end": v(37.05, 90.72) * mm});
            skLineSegment(sketch, "E79.1", {"start": v(37.05, 90.72) * mm, "end": v(35.18, 93.97) * mm});
            skLineSegment(sketch, "E79.2", {"start": v(35.18, 93.97) * mm, "end": v(37.05, 97.22) * mm});
            skLineSegment(sketch, "E79.3", {"start": v(37.05, 97.22) * mm, "end": v(40.8, 97.22) * mm});
            skLineSegment(sketch, "E79.4", {"start": v(40.8, 97.22) * mm, "end": v(42.67, 93.97) * mm});
            skLineSegment(sketch, "E79.5", {"start": v(42.67, 93.97) * mm, "end": v(40.8, 90.72) * mm});
            skPoint(sketch, "E79.0.midPoint", {"position": v(38.92, 90.72) * mm});
            skLineSegment(sketch, "E80", {"start": v(-90.8, -40.76) * mm, "end": v(-40.71, -90.87) * mm});
            skLineSegment(sketch, "E81", {"start": v(-36.24, -92.42) * mm, "end": v(36.24, -92.42) * mm});
            skLineSegment(sketch, "E82", {"start": v(40.71, -90.87) * mm, "end": v(90.72, -40.8) * mm});
            skLineSegment(sketch, "E83", {"start": v(92.34, -36.1) * mm, "end": v(92.34, 36.1) * mm});
            skLineSegment(sketch, "E84", {"start": v(90.72, 40.8) * mm, "end": v(40.8, 90.72) * mm});
            skLineSegment(sketch, "E85", {"start": v(36.11, 92.35) * mm, "end": v(-36.11, 92.35) * mm});
            skLineSegment(sketch, "E86", {"start": v(-40.8, 90.72) * mm, "end": v(-90.8, 40.76) * mm});
            skLineSegment(sketch, "E87", {"start": v(-92.38, 36.17) * mm, "end": v(-92.38, -36.17) * mm});
            skSolve(sketch);
        }
        {
            var Q0;
            Q0 = qSketchRegion(id + "F30", true);
            extrude(context, id + "F31", {"entities" : qUnion([Q0]), "depth" : 7.87 * mm});
        }
        {
            var Q0;
            Q0=qCreatedBy(id+"F21.planeOp",FACE);
            var sketch = newSketch(context, id + "F32", { "sketchPlane" : qUnion([Q0])});
            skLineSegment(sketch, "E88.0", {"start": v(-67.24, -27.85) * mm, "end": v(-67.24, 27.85) * mm});
            skLineSegment(sketch, "E88.1", {"start": v(-67.24, 27.85) * mm, "end": v(-27.85, 67.24) * mm});
            skLineSegment(sketch, "E88.2", {"start": v(-27.85, 67.24) * mm, "end": v(27.85, 67.24) * mm});
            skLineSegment(sketch, "E88.3", {"start": v(27.85, 67.24) * mm, "end": v(67.24, 27.85) * mm});
            skLineSegment(sketch, "E88.4", {"start": v(67.24, 27.85) * mm, "end": v(67.24, -27.85) * mm});
            skLineSegment(sketch, "E88.5", {"start": v(67.24, -27.85) * mm, "end": v(27.85, -67.24) * mm});
            skLineSegment(sketch, "E88.6", {"start": v(27.85, -67.24) * mm, "end": v(-27.85, -67.24) * mm});
            skLineSegment(sketch, "E88.7", {"start": v(-27.85, -67.24) * mm, "end": v(-67.24, -27.85) * mm});
            skPoint(sketch, "E88.0.midPoint", {"position": v(-67.24, 0) * mm});
            skCircle(sketch, "E89.cCircle", {"center": v(67.24, -27.85) * mm, "radius": 3.35 * mm, "construction": true});
            skLineSegment(sketch, "E89.0", {"start": v(70.59, -25.92) * mm, "end": v(70.59, -29.78) * mm});
            skLineSegment(sketch, "E89.1", {"start": v(70.59, -29.78) * mm, "end": v(67.24, -31.72) * mm});
            skLineSegment(sketch, "E89.2", {"start": v(67.24, -31.72) * mm, "end": v(63.89, -29.78) * mm});
            skLineSegment(sketch, "E89.3", {"start": v(63.89, -29.78) * mm, "end": v(63.89, -25.92) * mm});
            skLineSegment(sketch, "E89.4", {"start": v(63.89, -25.92) * mm, "end": v(67.24, -23.98) * mm});
            skLineSegment(sketch, "E89.5", {"start": v(67.24, -23.98) * mm, "end": v(70.59, -25.92) * mm});
            skPoint(sketch, "E89.0.midPoint", {"position": v(70.59, -27.85) * mm});
            skCircle(sketch, "E90.cCircle", {"center": v(67.24, 27.85) * mm, "radius": 3.35 * mm, "construction": true});
            skLineSegment(sketch, "E90.0", {"start": v(70.59, 29.78) * mm, "end": v(70.59, 25.92) * mm});
            skLineSegment(sketch, "E90.1", {"start": v(70.59, 25.92) * mm, "end": v(67.24, 23.98) * mm});
            skLineSegment(sketch, "E90.2", {"start": v(67.24, 23.98) * mm, "end": v(63.89, 25.92) * mm});
            skLineSegment(sketch, "E90.3", {"start": v(63.89, 25.92) * mm, "end": v(63.89, 29.78) * mm});
            skLineSegment(sketch, "E90.4", {"start": v(63.89, 29.78) * mm, "end": v(67.24, 31.72) * mm});
            skLineSegment(sketch, "E90.5", {"start": v(67.24, 31.72) * mm, "end": v(70.59, 29.78) * mm});
            skPoint(sketch, "E90.0.midPoint", {"position": v(70.59, 27.85) * mm});
            skCircle(sketch, "E91.cCircle", {"center": v(27.85, 67.24) * mm, "radius": 3.12 * mm, "construction": true});
            skLineSegment(sketch, "E91.0", {"start": v(26.05, 70.36) * mm, "end": v(29.65, 70.36) * mm});
            skLineSegment(sketch, "E91.1", {"start": v(29.65, 70.36) * mm, "end": v(31.46, 67.24) * mm});
            skLineSegment(sketch, "E91.2", {"start": v(31.46, 67.24) * mm, "end": v(29.65, 64.11) * mm});
            skLineSegment(sketch, "E91.3", {"start": v(29.65, 64.11) * mm, "end": v(26.05, 64.11) * mm});
            skLineSegment(sketch, "E91.4", {"start": v(26.05, 64.11) * mm, "end": v(24.24, 67.24) * mm});
            skLineSegment(sketch, "E91.5", {"start": v(24.24, 67.24) * mm, "end": v(26.05, 70.36) * mm});
            skPoint(sketch, "E91.0.midPoint", {"position": v(27.85, 70.36) * mm});
            skCircle(sketch, "E92.cCircle", {"center": v(-27.85, 67.24) * mm, "radius": 3.12 * mm, "construction": true});
            skLineSegment(sketch, "E92.0", {"start": v(-29.65, 70.36) * mm, "end": v(-26.05, 70.36) * mm});
            skLineSegment(sketch, "E92.1", {"start": v(-26.05, 70.36) * mm, "end": v(-24.24, 67.24) * mm});
            skLineSegment(sketch, "E92.2", {"start": v(-24.24, 67.24) * mm, "end": v(-26.05, 64.11) * mm});
            skLineSegment(sketch, "E92.3", {"start": v(-26.05, 64.11) * mm, "end": v(-29.65, 64.11) * mm});
            skLineSegment(sketch, "E92.4", {"start": v(-29.65, 64.11) * mm, "end": v(-31.46, 67.24) * mm});
            skLineSegment(sketch, "E92.5", {"start": v(-31.46, 67.24) * mm, "end": v(-29.65, 70.36) * mm});
            skPoint(sketch, "E92.0.midPoint", {"position": v(-27.85, 70.36) * mm});
            skCircle(sketch, "E93.cCircle", {"center": v(27.85, -67.24) * mm, "radius": 3.13 * mm, "construction": true});
            skLineSegment(sketch, "E93.0", {"start": v(29.66, -70.37) * mm, "end": v(26.04, -70.37) * mm});
            skLineSegment(sketch, "E93.1", {"start": v(26.04, -70.37) * mm, "end": v(24.23, -67.24) * mm});
            skLineSegment(sketch, "E93.2", {"start": v(24.23, -67.24) * mm, "end": v(26.04, -64.1) * mm});
            skLineSegment(sketch, "E93.3", {"start": v(26.04, -64.1) * mm, "end": v(29.66, -64.1) * mm});
            skLineSegment(sketch, "E93.4", {"start": v(29.66, -64.1) * mm, "end": v(31.47, -67.24) * mm});
            skLineSegment(sketch, "E93.5", {"start": v(31.47, -67.24) * mm, "end": v(29.66, -70.37) * mm});
            skPoint(sketch, "E93.0.midPoint", {"position": v(27.85, -70.37) * mm});
            skCircle(sketch, "E94.cCircle", {"center": v(-27.85, -67.24) * mm, "radius": 3.13 * mm, "construction": true});
            skLineSegment(sketch, "E94.0", {"start": v(-26.04, -70.37) * mm, "end": v(-29.66, -70.37) * mm});
            skLineSegment(sketch, "E94.1", {"start": v(-29.66, -70.37) * mm, "end": v(-31.47, -67.24) * mm});
            skLineSegment(sketch, "E94.2", {"start": v(-31.47, -67.24) * mm, "end": v(-29.66, -64.1) * mm});
            skLineSegment(sketch, "E94.3", {"start": v(-29.66, -64.1) * mm, "end": v(-26.04, -64.1) * mm});
            skLineSegment(sketch, "E94.4", {"start": v(-26.04, -64.1) * mm, "end": v(-24.23, -67.24) * mm});
            skLineSegment(sketch, "E94.5", {"start": v(-24.23, -67.24) * mm, "end": v(-26.04, -70.37) * mm});
            skPoint(sketch, "E94.0.midPoint", {"position": v(-27.85, -70.37) * mm});
            skCircle(sketch, "E95.cCircle", {"center": v(-67.24, -27.85) * mm, "radius": 3.44 * mm, "construction": true});
            skLineSegment(sketch, "E95.0", {"start": v(-70.68, -29.84) * mm, "end": v(-70.68, -25.86) * mm});
            skLineSegment(sketch, "E95.1", {"start": v(-70.68, -25.86) * mm, "end": v(-67.24, -23.88) * mm});
            skLineSegment(sketch, "E95.2", {"start": v(-67.24, -23.88) * mm, "end": v(-63.8, -25.86) * mm});
            skLineSegment(sketch, "E95.3", {"start": v(-63.8, -25.86) * mm, "end": v(-63.8, -29.84) * mm});
            skLineSegment(sketch, "E95.4", {"start": v(-63.8, -29.84) * mm, "end": v(-67.24, -31.82) * mm});
            skLineSegment(sketch, "E95.5", {"start": v(-67.24, -31.82) * mm, "end": v(-70.68, -29.84) * mm});
            skPoint(sketch, "E95.0.midPoint", {"position": v(-70.68, -27.85) * mm});
            skCircle(sketch, "E96.cCircle", {"center": v(-67.24, 27.85) * mm, "radius": 3.44 * mm, "construction": true});
            skLineSegment(sketch, "E96.0", {"start": v(-70.68, 25.86) * mm, "end": v(-70.68, 29.84) * mm});
            skLineSegment(sketch, "E96.1", {"start": v(-70.68, 29.84) * mm, "end": v(-67.24, 31.82) * mm});
            skLineSegment(sketch, "E96.2", {"start": v(-67.24, 31.82) * mm, "end": v(-63.8, 29.84) * mm});
            skLineSegment(sketch, "E96.3", {"start": v(-63.8, 29.84) * mm, "end": v(-63.8, 25.86) * mm});
            skLineSegment(sketch, "E96.4", {"start": v(-63.8, 25.86) * mm, "end": v(-67.24, 23.88) * mm});
            skLineSegment(sketch, "E96.5", {"start": v(-67.24, 23.88) * mm, "end": v(-70.68, 25.86) * mm});
            skPoint(sketch, "E96.0.midPoint", {"position": v(-70.68, 27.85) * mm});
            skLineSegment(sketch, "E97", {"start": v(-26.04, -64.1) * mm, "end": v(26.04, -64.1) * mm});
            skLineSegment(sketch, "E98", {"start": v(26.04, -64.1) * mm, "end": v(63.89, -25.92) * mm});
            skLineSegment(sketch, "E99", {"start": v(63.89, -25.92) * mm, "end": v(63.89, 25.92) * mm});
            skLineSegment(sketch, "E100", {"start": v(63.89, 25.92) * mm, "end": v(26.05, 64.11) * mm});
            skLineSegment(sketch, "E101", {"start": v(26.05, 64.11) * mm, "end": v(-26.05, 64.11) * mm});
            skLineSegment(sketch, "E102", {"start": v(-26.05, 64.11) * mm, "end": v(-63.8, 25.86) * mm});
            skLineSegment(sketch, "E103", {"start": v(-63.8, 25.86) * mm, "end": v(-63.8, -25.86) * mm});
            skLineSegment(sketch, "E104", {"start": v(-63.8, -25.86) * mm, "end": v(-26.04, -64.1) * mm});
            skSolve(sketch);
        }
        {
            var Q0;
            Q0 = qSketchRegion(id + "F32", true);
            extrude(context, id + "F33", {"entities" : qUnion([Q0]), "depth" : 22.1 * mm});
        }
        {
            var Q0;
            Q0=qCreatedBy(id+"F21.planeOp",FACE);
            cPlane(context, id + "F34", {"entities" : qUnion([Q0]), "cplaneType" : CPlaneType.OFFSET, "offset" : 21.84 * mm, "width" : 152.4 * mm, "height" : 152.4 * mm});
        }
        {
            var Q0;
            Q0=qCreatedBy(id+"F34.planeOp",FACE);
            var sketch = newSketch(context, id + "F35", { "sketchPlane" : qUnion([Q0])});
            skCircle(sketch, "E105.cCircle", {"center": v(0, 0) * mm, "radius": 70.74 * mm, "construction": true});
            skLineSegment(sketch, "E105.0", {"start": v(29.3, -70.74) * mm, "end": v(-29.3, -70.74) * mm});
            skLineSegment(sketch, "E105.1", {"start": v(-29.3, -70.74) * mm, "end": v(-70.74, -29.3) * mm});
            skLineSegment(sketch, "E105.2", {"start": v(-70.74, -29.3) * mm, "end": v(-70.74, 29.3) * mm});
            skLineSegment(sketch, "E105.3", {"start": v(-70.74, 29.3) * mm, "end": v(-29.3, 70.74) * mm});
            skLineSegment(sketch, "E105.4", {"start": v(-29.3, 70.74) * mm, "end": v(29.3, 70.74) * mm});
            skLineSegment(sketch, "E105.5", {"start": v(29.3, 70.74) * mm, "end": v(70.74, 29.3) * mm});
            skLineSegment(sketch, "E105.6", {"start": v(70.74, 29.3) * mm, "end": v(70.74, -29.3) * mm});
            skLineSegment(sketch, "E105.7", {"start": v(70.74, -29.3) * mm, "end": v(29.3, -70.74) * mm});
            skPoint(sketch, "E105.0.midPoint", {"position": v(0, -70.74) * mm});
            skCircle(sketch, "E106.cCircle", {"center": v(0, 0) * mm, "radius": 43.18 * mm, "construction": true});
            skLineSegment(sketch, "E106.0", {"start": v(17.89, -43.18) * mm, "end": v(-17.89, -43.18) * mm});
            skLineSegment(sketch, "E106.1", {"start": v(-17.89, -43.18) * mm, "end": v(-43.18, -17.89) * mm});
            skLineSegment(sketch, "E106.2", {"start": v(-43.18, -17.89) * mm, "end": v(-43.18, 17.89) * mm});
            skLineSegment(sketch, "E106.3", {"start": v(-43.18, 17.89) * mm, "end": v(-17.89, 43.18) * mm});
            skLineSegment(sketch, "E106.4", {"start": v(-17.89, 43.18) * mm, "end": v(17.89, 43.18) * mm});
            skLineSegment(sketch, "E106.5", {"start": v(17.89, 43.18) * mm, "end": v(43.18, 17.89) * mm});
            skLineSegment(sketch, "E106.6", {"start": v(43.18, 17.89) * mm, "end": v(43.18, -17.89) * mm});
            skLineSegment(sketch, "E106.7", {"start": v(43.18, -17.89) * mm, "end": v(17.89, -43.18) * mm});
            skPoint(sketch, "E106.0.midPoint", {"position": v(0, -43.18) * mm});
            skSolve(sketch);
        }
        {
            var Q0;
            Q0 = qSketchRegion(id + "F35", true);
            extrude(context, id + "F36", {"entities" : qUnion([Q0]), "operationType" : NewBodyOperationType.ADD, "depth" : 3.56 * mm});
        }
        {
            var Q0;
            Q0=qCreatedBy(makeId("Front.planeOp"),FACE);
            var sketch = newSketch(context, id + "F37", { "sketchPlane" : qUnion([Q0])});
            skPoint(sketch, "E107.0.midPoint", {"position": v(0, 189.03) * mm});
            skLineSegment(sketch, "E108.left", {"start": v(-70.52, 163.7) * mm, "end": v(-70.52, 163.7) * mm});
            skLineSegment(sketch, "E108.right", {"start": v(70.52, 163.7) * mm, "end": v(70.52, 163.7) * mm});
            skPoint(sketch, "E108.middle", {"position": v(0, 163.7) * mm});
            skLineSegment(sketch, "E109", {"start": v(-29.24, 163.7) * mm, "end": v(-29.24, 182.4) * mm});
            skLineSegment(sketch, "E110", {"start": v(-29.24, 182.4) * mm, "end": v(-70.52, 163.7) * mm});
            skLineSegment(sketch, "E111", {"start": v(29.24, 182.4) * mm, "end": v(70.52, 163.7) * mm});
            skLineSegment(sketch, "E112", {"start": v(29.24, 182.4) * mm, "end": v(29.24, 163.7) * mm});
            skLineSegment(sketch, "E113", {"start": v(29.24, 163.7) * mm, "end": v(70.52, 163.7) * mm});
            skLineSegment(sketch, "E114", {"start": v(-70.52, 163.7) * mm, "end": v(-29.24, 163.7) * mm});
            skSolve(sketch);
        }
        {
            var Q0;
            Q0 = qSketchRegion(id + "F37", true);
            extrude(context, id + "F38", {"entities" : qUnion([Q0]), "endBound" : BoundingType.SYMMETRIC, "depth" : 58.42 * mm});
        }
        {
            var Q0;
            Q0=qCreatedBy(makeId("Right.planeOp"),FACE);
            var sketch = newSketch(context, id + "F39", { "sketchPlane" : qUnion([Q0])});
            skPoint(sketch, "E115.0.midPoint", {"position": v(0, 188.96) * mm});
            skLineSegment(sketch, "E116.bottom", {"start": v(70.71, 163.3) * mm, "end": v(-70.71, 163.3) * mm});
            skLineSegment(sketch, "E116.top", {"start": v(70.71, 163.3) * mm, "end": v(-70.71, 163.3) * mm});
            skLineSegment(sketch, "E116.left", {"start": v(70.71, 163.3) * mm, "end": v(70.71, 163.3) * mm});
            skLineSegment(sketch, "E116.right", {"start": v(-70.71, 163.3) * mm, "end": v(-70.71, 163.3) * mm});
            skPoint(sketch, "E116.middle", {"position": v(0, 163.3) * mm});
            skLineSegment(sketch, "E117", {"start": v(-29.2, 182.35) * mm, "end": v(-29.2, 163.3) * mm});
            skLineSegment(sketch, "E118", {"start": v(29.2, 182.35) * mm, "end": v(29.2, 163.3) * mm});
            skLineSegment(sketch, "E119", {"start": v(-70.71, 163.3) * mm, "end": v(-29.2, 163.3) * mm});
            skLineSegment(sketch, "E120", {"start": v(-70.71, 163.3) * mm, "end": v(-29.2, 182.35) * mm});
            skLineSegment(sketch, "E121", {"start": v(29.2, 182.35) * mm, "end": v(70.71, 163.3) * mm});
            skSolve(sketch);
        }
        {
            var Q0;
            Q0 = qSketchRegion(id + "F39", true);
            extrude(context, id + "F40", {"entities" : qUnion([Q0]), "endBound" : BoundingType.SYMMETRIC, "depth" : 58.93 * mm});
        }
        {
            var Q0;
            Q0 = qSketchRegion(id + "F37", true);
            extrude(context, id + "F41", {"entities" : qUnion([Q0]), "depth" : 25.4 * mm});
        }
        {
            var Q0;
            Q0=qCreatedBy(id+"F34.planeOp",FACE);
            var sketch = newSketch(context, id + "F42", { "sketchPlane" : qUnion([Q0])});
            skCircle(sketch, "E122.cCircle", {"center": v(0, 0) * mm, "radius": 57.6 * mm, "construction": true});
            skLineSegment(sketch, "E122.0", {"start": v(57.6, 23.86) * mm, "end": v(57.6, -23.86) * mm});
            skLineSegment(sketch, "E122.1", {"start": v(57.6, -23.86) * mm, "end": v(23.86, -57.6) * mm});
            skLineSegment(sketch, "E122.2", {"start": v(23.86, -57.6) * mm, "end": v(-23.86, -57.6) * mm});
            skLineSegment(sketch, "E122.3", {"start": v(-23.86, -57.6) * mm, "end": v(-57.6, -23.86) * mm});
            skLineSegment(sketch, "E122.4", {"start": v(-57.6, -23.86) * mm, "end": v(-57.6, 23.86) * mm});
            skLineSegment(sketch, "E122.5", {"start": v(-57.6, 23.86) * mm, "end": v(-23.86, 57.6) * mm});
            skLineSegment(sketch, "E122.6", {"start": v(-23.86, 57.6) * mm, "end": v(23.86, 57.6) * mm});
            skLineSegment(sketch, "E122.7", {"start": v(23.86, 57.6) * mm, "end": v(57.6, 23.86) * mm});
            skPoint(sketch, "E122.0.midPoint", {"position": v(57.6, 0) * mm});
            skCircle(sketch, "E123.cCircle", {"center": v(0, 0) * mm, "radius": 61.43 * mm, "construction": true});
            skPoint(sketch, "E123.cCircle.perimeterSnap0", {"position": v(-57.6, 0) * mm});
            skLineSegment(sketch, "E123.0", {"start": v(-61.43, -25.45) * mm, "end": v(-61.43, 25.45) * mm});
            skLineSegment(sketch, "E123.1", {"start": v(-61.43, 25.45) * mm, "end": v(-25.45, 61.43) * mm});
            skLineSegment(sketch, "E123.2", {"start": v(-25.45, 61.43) * mm, "end": v(25.45, 61.43) * mm});
            skLineSegment(sketch, "E123.3", {"start": v(25.45, 61.43) * mm, "end": v(61.43, 25.45) * mm});
            skLineSegment(sketch, "E123.4", {"start": v(61.43, 25.45) * mm, "end": v(61.43, -25.45) * mm});
            skLineSegment(sketch, "E123.5", {"start": v(61.43, -25.45) * mm, "end": v(25.45, -61.43) * mm});
            skLineSegment(sketch, "E123.6", {"start": v(25.45, -61.43) * mm, "end": v(-25.45, -61.43) * mm});
            skLineSegment(sketch, "E123.7", {"start": v(-25.45, -61.43) * mm, "end": v(-61.43, -25.45) * mm});
            skPoint(sketch, "E123.0.midPoint", {"position": v(-61.43, 0) * mm});
            skPoint(sketch, "E123.0.midPoint.positionSnap0", {"position": v(-57.6, 0) * mm});
            skSolve(sketch);
        }
        {
            var Q0;
            Q0 = qSketchRegion(id + "F42", true);
            extrude(context, id + "F43", {"entities" : qUnion([Q0]), "depth" : 7.62 * mm});
        }
        {
            var Q0;
            Q0=qCreatedBy(id+"F34.planeOp",FACE);
            var sketch = newSketch(context, id + "F44", { "sketchPlane" : qUnion([Q0])});
            skPoint(sketch, "E124.0.midPoint", {"position": v(-40.84, 40.66) * mm});
            skPoint(sketch, "E125.0.midPoint", {"position": v(0, 54.02) * mm});
            skLineSegment(sketch, "E126", {"start": v(52.63, -28.82) * mm, "end": v(47.58, -28.82) * mm});
            skLineSegment(sketch, "E127", {"start": v(29.57, -51.99) * mm, "end": v(29.57, -46.84) * mm});
            skLineSegment(sketch, "E128", {"start": v(52.3, 29.26) * mm, "end": v(47.14, 29.26) * mm});
            skLineSegment(sketch, "E129", {"start": v(47.14, 29.26) * mm, "end": v(52.3, 29.26) * mm});
            skLineSegment(sketch, "E130", {"start": v(29.46, 52) * mm, "end": v(29.46, 46.95) * mm});
            skLineSegment(sketch, "E131", {"start": v(-29.43, 46.97) * mm, "end": v(-29.43, 52.13) * mm});
            skLineSegment(sketch, "E132", {"start": v(-47.2, 29.2) * mm, "end": v(-52.24, 29.2) * mm});
            skLineSegment(sketch, "E133", {"start": v(-52.24, 29.2) * mm, "end": v(-47.2, 29.2) * mm});
            skLineSegment(sketch, "E134", {"start": v(-47.2, -29.2) * mm, "end": v(-52.24, -29.2) * mm});
            skLineSegment(sketch, "E135", {"start": v(-29.46, -46.94) * mm, "end": v(-29.46, -52) * mm});
            skLineSegment(sketch, "E136", {"start": v(-29.46, -52) * mm, "end": v(-29.46, -45.28) * mm});
            skLineSegment(sketch, "E137", {"start": v(29.57, -51.99) * mm, "end": v(52.63, -28.82) * mm});
            skLineSegment(sketch, "E138", {"start": v(47.58, -28.82) * mm, "end": v(29.57, -46.84) * mm});
            skLineSegment(sketch, "E139", {"start": v(47.14, 29.26) * mm, "end": v(29.46, 46.95) * mm});
            skLineSegment(sketch, "E140", {"start": v(52.3, 29.26) * mm, "end": v(29.46, 52) * mm});
            skLineSegment(sketch, "E141", {"start": v(29.46, 46.95) * mm, "end": v(47.14, 29.26) * mm});
            skLineSegment(sketch, "E142", {"start": v(-52.24, 29.2) * mm, "end": v(-29.43, 52.13) * mm});
            skLineSegment(sketch, "E143", {"start": v(-29.43, 46.97) * mm, "end": v(-47.2, 29.2) * mm});
            skLineSegment(sketch, "E144", {"start": v(-52.24, -29.2) * mm, "end": v(-29.46, -52) * mm});
            skLineSegment(sketch, "E145", {"start": v(-47.2, -29.2) * mm, "end": v(-29.46, -46.94) * mm});
            skSolve(sketch);
        }
        {
            var Q0;
            Q0 = qSketchRegion(id + "F44", true);
            extrude(context, id + "F45", {"entities" : qUnion([Q0]), "depth" : 11.94 * mm});
        }
        {
            var Q0;
            Q0=qCreatedBy(id+"F34.planeOp",FACE);
            var sketch = newSketch(context, id + "F46", { "sketchPlane" : qUnion([Q0])});
            skLineSegment(sketch, "E146", {"start": v(-47.23, 29.16) * mm, "end": v(-29.4, 46.93) * mm});
            skLineSegment(sketch, "E147", {"start": v(-29.4, 46.93) * mm, "end": v(-29.4, 42.28) * mm});
            skLineSegment(sketch, "E148", {"start": v(-29.4, 42.28) * mm, "end": v(-42.6, 29.16) * mm});
            skLineSegment(sketch, "E149", {"start": v(-47.23, 29.16) * mm, "end": v(-42.6, 29.16) * mm});
            skLineSegment(sketch, "E150", {"start": v(-47.23, -29.1) * mm, "end": v(-42.6, -29.1) * mm});
            skLineSegment(sketch, "E151", {"start": v(-42.6, -29.1) * mm, "end": v(-29.4, -42.37) * mm});
            skLineSegment(sketch, "E152", {"start": v(-29.4, -42.37) * mm, "end": v(-29.4, -46.79) * mm});
            skLineSegment(sketch, "E153", {"start": v(-29.4, -46.79) * mm, "end": v(-47.23, -29.1) * mm});
            skLineSegment(sketch, "E154", {"start": v(29.45, 47.07) * mm, "end": v(47.17, 29.34) * mm});
            skLineSegment(sketch, "E155", {"start": v(29.45, 42.28) * mm, "end": v(42.87, 29.34) * mm});
            skLineSegment(sketch, "E156", {"start": v(29.45, 47.07) * mm, "end": v(29.45, 42.28) * mm});
            skLineSegment(sketch, "E157", {"start": v(42.87, 29.34) * mm, "end": v(47.17, 29.34) * mm});
            skLineSegment(sketch, "E158", {"start": v(47.17, -29.43) * mm, "end": v(29.45, -47.13) * mm});
            skLineSegment(sketch, "E159", {"start": v(42.87, -29.43) * mm, "end": v(29.45, -42.83) * mm});
            skLineSegment(sketch, "E160", {"start": v(42.87, -29.43) * mm, "end": v(47.17, -29.43) * mm});
            skLineSegment(sketch, "E161", {"start": v(29.45, -42.83) * mm, "end": v(29.45, -47.13) * mm});
            skSolve(sketch);
        }
        {
            var Q0;
            Q0 = qSketchRegion(id + "F46", true);
            extrude(context, id + "F47", {"entities" : qUnion([Q0]), "depth" : 14.48 * mm});
        }
        {
            var Q0;
            Q0=qCreatedBy(id+"F34.planeOp",FACE);
            cPlane(context, id + "F48", {"entities" : qUnion([Q0]), "cplaneType" : CPlaneType.OFFSET, "offset" : 14.48 * mm, "width" : 152.4 * mm, "height" : 152.4 * mm});
        }
        {
            var Q0;
            Q0=qCreatedBy(id+"F48.planeOp",FACE);
            var sketch = newSketch(context, id + "F49", { "sketchPlane" : qUnion([Q0])});
            skPoint(sketch, "E162.0.midPoint", {"position": v(-35.87, 35.88) * mm});
            skPoint(sketch, "E163.0.midPoint", {"position": v(0, 29.06) * mm});
            skLineSegment(sketch, "E164", {"start": v(0, 29.06) * mm, "end": v(-28.05, 43.7) * mm});
            skLineSegment(sketch, "E165", {"start": v(0, 29.06) * mm, "end": v(29.23, 42.52) * mm});
            skLineSegment(sketch, "E166", {"start": v(29.06, 0) * mm, "end": v(43.03, 28.71) * mm});
            skLineSegment(sketch, "E167", {"start": v(-29.06, 0) * mm, "end": v(-42.84, 28.91) * mm});
            skLineSegment(sketch, "E168", {"start": v(-29.06, 0) * mm, "end": v(-42.7, -29.05) * mm});
            skLineSegment(sketch, "E169", {"start": v(0, -29.06) * mm, "end": v(-28.62, -43.13) * mm});
            skLineSegment(sketch, "E170", {"start": v(0, -29.06) * mm, "end": v(28.84, -42.9) * mm});
            skLineSegment(sketch, "E171", {"start": v(29.06, 0) * mm, "end": v(43.29, -28.46) * mm});
            skLineSegment(sketch, "E172", {"start": v(-42.7, -29.05) * mm, "end": v(-28.62, -43.13) * mm});
            skLineSegment(sketch, "E173", {"start": v(28.84, -42.9) * mm, "end": v(43.29, -28.46) * mm});
            skLineSegment(sketch, "E174", {"start": v(43.03, 28.71) * mm, "end": v(29.23, 42.52) * mm});
            skLineSegment(sketch, "E175", {"start": v(-28.05, 43.7) * mm, "end": v(-42.84, 28.91) * mm});
            skSolve(sketch);
        }
        {
            var Q0;
            Q0 = qSketchRegion(id + "F49", true);
            extrude(context, id + "F50", {"entities" : qUnion([Q0]), "depth" : 1.52 * mm});
        }
        {
            var Q0;
            Q0=qCreatedBy(id+"F48.planeOp",FACE);
            cPlane(context, id + "F51", {"entities" : qUnion([Q0]), "cplaneType" : CPlaneType.OFFSET, "offset" : 1.52 * mm, "width" : 152.4 * mm, "height" : 152.4 * mm});
        }
        {
            var Q0;
            Q0=qCreatedBy(id+"F51.planeOp",FACE);
            var sketch = newSketch(context, id + "F52", { "sketchPlane" : qUnion([Q0])});
            skLineSegment(sketch, "E176.bottom", {"start": v(-29.15, 29.2) * mm, "end": v(29.15, 29.2) * mm});
            skLineSegment(sketch, "E176.top", {"start": v(-29.15, -29.2) * mm, "end": v(29.15, -29.2) * mm});
            skLineSegment(sketch, "E176.left", {"start": v(-29.15, 29.2) * mm, "end": v(-29.15, -29.2) * mm});
            skLineSegment(sketch, "E176.right", {"start": v(29.15, 29.2) * mm, "end": v(29.15, -29.2) * mm});
            skPoint(sketch, "E176.middle", {"position": v(0, 0) * mm});
            skSolve(sketch);
        }
        {
            var Q0;
            Q0 = qSketchRegion(id + "F52", true);
            extrude(context, id + "F53", {"entities" : qUnion([Q0]), "depth" : 7.87 * mm});
        }
    });
